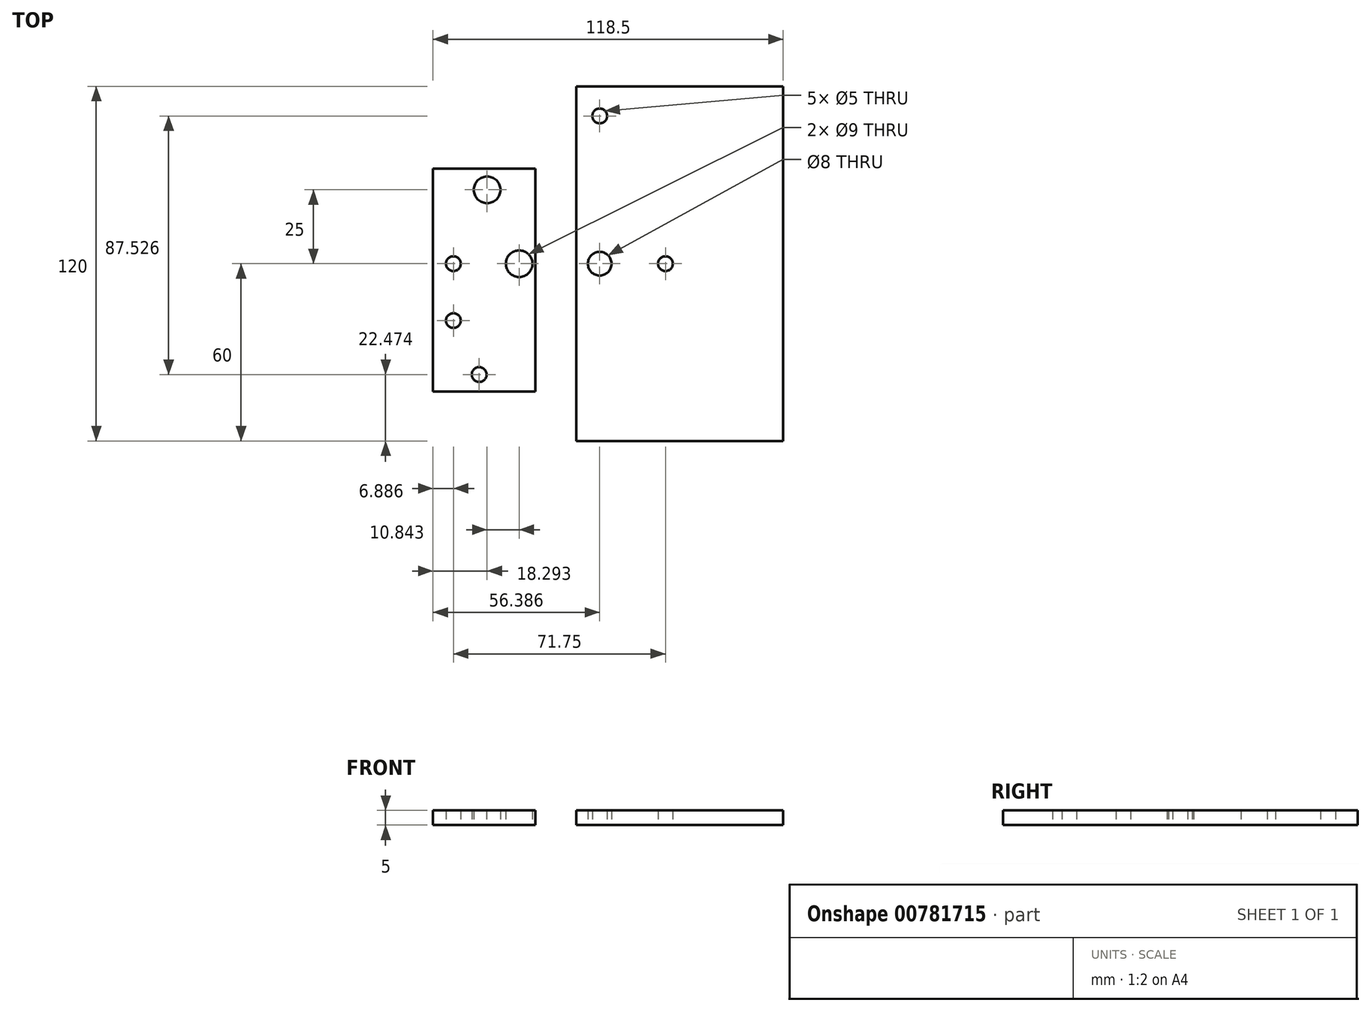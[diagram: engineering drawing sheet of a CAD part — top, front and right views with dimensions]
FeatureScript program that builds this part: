
annotation { "Feature Type Name" : "Feature", "Feature Type Description" : "" }
export const myFeature = defineFeature(function(context is Context, id is Id, definition is map)
    precondition{}
    {
        {
            var Q0;
            Q0=qCreatedBy(makeId("Top.planeOp"),FACE);
            var sketch = newSketch(context, id + "F0", { "sketchPlane" : qUnion([Q0])});
            skLineSegment(sketch, "E0.bottom", {"start": v(-20, 60) * mm, "end": v(50, 60) * mm});
            skLineSegment(sketch, "E0.top", {"start": v(-20, -60) * mm, "end": v(50, -60) * mm});
            skLineSegment(sketch, "E0.left", {"start": v(-20, 60) * mm, "end": v(-20, -60) * mm});
            skLineSegment(sketch, "E0.right", {"start": v(50, 60) * mm, "end": v(50, -60) * mm});
            skSolve(sketch);
        }
        {
            var Q0;
            Q0=makeQuery(id+"F0.imprint","IMPRINT",FACE,{"disambiguationData":[TD([[makeQuery(id+"F0.imprint","IMPRINT",EDGE,{"derivedFrom":sQuery(id+"F0.wireOp",EDGE,"E0.bottom")}),-1.0]])]});
            var sketch = newSketch(context, id + "F1", { "sketchPlane" : qUnion([Q0])});
            skCircle(sketch, "E1", {"center": v(-12.11, 0) * mm, "radius": 4 * mm});
            skSolve(sketch);
        }
        {
            var Q0;
            Q0=makeQuery(id+"F0.imprint","IMPRINT",FACE,{"disambiguationData":[TD([[makeQuery(id+"F0.imprint","IMPRINT",EDGE,{"derivedFrom":sQuery(id+"F0.wireOp",EDGE,"E0.bottom")}),-1.0]])]});
            var sketch = newSketch(context, id + "F2", { "sketchPlane" : qUnion([Q0])});
            skCircle(sketch, "E2", {"center": v(10.14, 0) * mm, "radius": 2.5 * mm});
            skSolve(sketch);
        }
        {
            var Q0;
            Q0=qCreatedBy(makeId("Top.planeOp"),FACE);
            var sketch = newSketch(context, id + "F3", { "sketchPlane" : qUnion([Q0])});
            skLineSegment(sketch, "E3.bottom", {"start": v(-68.5, 32.21) * mm, "end": v(-33.84, 32.21) * mm});
            skLineSegment(sketch, "E3.top", {"start": v(-68.5, -43.25) * mm, "end": v(-33.84, -43.25) * mm});
            skLineSegment(sketch, "E3.left", {"start": v(-68.5, 32.21) * mm, "end": v(-68.5, -43.25) * mm});
            skLineSegment(sketch, "E3.right", {"start": v(-33.84, 32.21) * mm, "end": v(-33.84, -43.25) * mm});
            skSolve(sketch);
        }
        {
            var Q0;
            Q0=makeQuery(id+"F0.imprint","IMPRINT",FACE,{"disambiguationData":[TD([[makeQuery(id+"F0.imprint","IMPRINT",EDGE,{"derivedFrom":sQuery(id+"F0.wireOp",EDGE,"E0.bottom")}),-1.0]])]});
            var sketch = newSketch(context, id + "F4", { "sketchPlane" : qUnion([Q0])});
            skCircle(sketch, "E4", {"center": v(-39.36, 0) * mm, "radius": 4.5 * mm});
            skSolve(sketch);
        }
        {
            var Q0;
            Q0=makeQuery(id+"F2.imprint","IMPRINT",FACE,{"disambiguationData":[TD([[makeQuery(id+"F2.imprint","IMPRINT",EDGE,{"derivedFrom":sQuery(id+"F2.wireOp",EDGE,"E2")}),-1.0]])]});
            var sketch = newSketch(context, id + "F5", { "sketchPlane" : qUnion([Q0])});
            skCircle(sketch, "E5", {"center": v(-12.11, 50) * mm, "radius": 2.5 * mm});
            skSolve(sketch);
        }
        {
            var Q0;
            Q0=makeQuery(id+"F4.imprint","IMPRINT",FACE,{"disambiguationData":[TD([[makeQuery(id+"F4.imprint","IMPRINT",EDGE,{"derivedFrom":sQuery(id+"F4.wireOp",EDGE,"E4")}),1.0]])]});
            var sketch = newSketch(context, id + "F6", { "sketchPlane" : qUnion([Q0])});
            skCircle(sketch, "E6", {"center": v(-61.61, 0) * mm, "radius": 2.5 * mm});
            skSolve(sketch);
        }
        {
            var Q0;
            Q0=qCreatedBy(makeId("Top.planeOp"),FACE);
            var sketch = newSketch(context, id + "F7", { "sketchPlane" : qUnion([Q0])});
            skCircle(sketch, "E7", {"center": v(-61.61, -19.25) * mm, "radius": 2.5 * mm});
            skSolve(sketch);
        }
        {
            var Q0;
            Q0=qCreatedBy(makeId("Top.planeOp"),FACE);
            var sketch = newSketch(context, id + "F8", { "sketchPlane" : qUnion([Q0])});
            skCircle(sketch, "E8", {"center": v(-50.2, 25) * mm, "radius": 4.5 * mm});
            skSolve(sketch);
        }
        {
            var Q0;
            Q0=makeQuery(id+"F3.imprint","IMPRINT",FACE,{"disambiguationData":[TD([[makeQuery(id+"F3.imprint","IMPRINT",EDGE,{"derivedFrom":sQuery(id+"F3.wireOp",EDGE,"E3.bottom")}),-1.0]])]});
            extrude(context, id + "F9", {"entities" : qUnion([Q0]), "depth" : 5 * mm, "offsetDistance" : 25 * mm});
        }
        {
            var Q0;
            Q0 = qSketchRegion(id + "F6", true);
            extrude(context, id + "F10", {"entities" : qUnion([Q0]), "operationType" : NewBodyOperationType.REMOVE, "depth" : 25 * mm, "offsetDistance" : 25 * mm});
        }
        {
            var Q0;
            Q0 = qSketchRegion(id + "F7", true);
            extrude(context, id + "F11", {"entities" : qUnion([Q0]), "operationType" : NewBodyOperationType.REMOVE, "oppositeDirection" : true, "depth" : 25 * mm, "offsetDistance" : 25 * mm});
        }
        {
            var Q0;
            Q0 = qSketchRegion(id + "F4", true);
            extrude(context, id + "F12", {"entities" : qUnion([Q0]), "operationType" : NewBodyOperationType.REMOVE, "depth" : 25 * mm, "offsetDistance" : 25 * mm});
        }
        {
            var Q0;
            Q0=makeQuery(id+"F0.imprint","IMPRINT",FACE,{"disambiguationData":[TD([[makeQuery(id+"F0.imprint","IMPRINT",EDGE,{"derivedFrom":sQuery(id+"F0.wireOp",EDGE,"E0.bottom")}),-1.0]])]});
            extrude(context, id + "F13", {"entities" : qUnion([Q0]), "depth" : 5 * mm, "offsetDistance" : 25 * mm});
        }
        {
            var Q0;
            Q0 = qSketchRegion(id + "F1", true);
            extrude(context, id + "F14", {"entities" : qUnion([Q0]), "operationType" : NewBodyOperationType.REMOVE, "depth" : 25 * mm, "offsetDistance" : 25 * mm});
        }
        {
            var Q0;
            Q0 = qSketchRegion(id + "F5", true);
            extrude(context, id + "F15", {"entities" : qUnion([Q0]), "operationType" : NewBodyOperationType.REMOVE, "depth" : 25 * mm, "offsetDistance" : 25 * mm});
        }
        {
            var Q0;
            Q0 = qSketchRegion(id + "F2", true);
            extrude(context, id + "F16", {"entities" : qUnion([Q0]), "operationType" : NewBodyOperationType.REMOVE, "depth" : 25 * mm, "offsetDistance" : 25 * mm});
        }
        {
            var Q0;
            Q0 = qSketchRegion(id + "F7", true);
            extrude(context, id + "F17", {"entities" : qUnion([Q0]), "operationType" : NewBodyOperationType.REMOVE, "depth" : 25 * mm, "offsetDistance" : 25 * mm});
        }
        {
            var Q0;
            Q0=makeQuery(id+"F8.imprint","IMPRINT",FACE,{"disambiguationData":[TD([[makeQuery(id+"F8.imprint","IMPRINT",EDGE,{"derivedFrom":sQuery(id+"F8.wireOp",EDGE,"E8")}),1.0]])]});
            extrude(context, id + "F18", {"entities" : qUnion([Q0]), "operationType" : NewBodyOperationType.REMOVE, "depth" : 25 * mm, "offsetDistance" : 25 * mm});
        }
        {
            var Q0;
            Q0=qCreatedBy(makeId("Top.planeOp"),FACE);
            var sketch = newSketch(context, id + "F19", { "sketchPlane" : qUnion([Q0])});
            skCircle(sketch, "E9", {"center": v(-52.9, -37.53) * mm, "radius": 2.5 * mm});
            skSolve(sketch);
        }
        {
            var Q0;
            Q0 = qSketchRegion(id + "F19", true);
            extrude(context, id + "F20", {"entities" : qUnion([Q0]), "operationType" : NewBodyOperationType.REMOVE, "depth" : 25 * mm, "offsetDistance" : 25 * mm});
        }
    });
